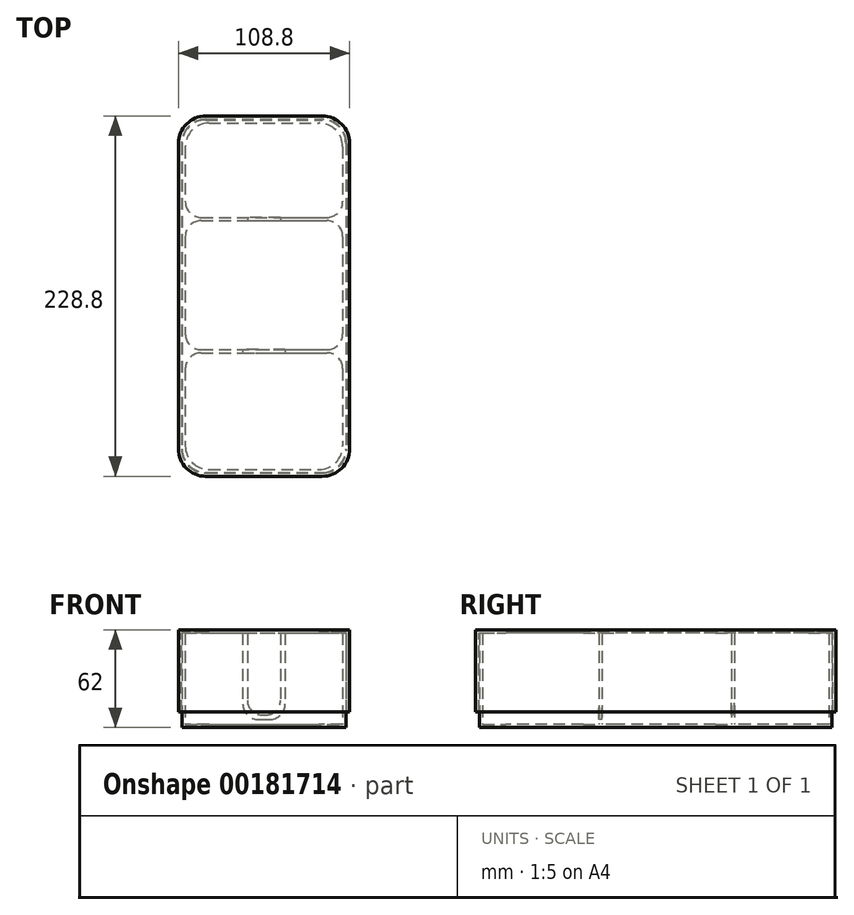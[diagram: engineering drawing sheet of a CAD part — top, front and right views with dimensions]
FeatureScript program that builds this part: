
annotation { "Feature Type Name" : "Feature", "Feature Type Description" : "" }
export const myFeature = defineFeature(function(context is Context, id is Id, definition is map)
    precondition{}
    {
        {
            var Q0;
            Q0=qCreatedBy(makeId("Top.planeOp"),FACE);
            var sketch = newSketch(context, id + "F0", { "sketchPlane" : qUnion([Q0])});
            skLineSegment(sketch, "E0.bottom", {"start": v(-39.51, 155.89) * mm, "end": v(30.49, 155.89) * mm});
            skLineSegment(sketch, "E0.top", {"start": v(-39.51, -64.11) * mm, "end": v(30.49, -64.11) * mm});
            skLineSegment(sketch, "E0.left", {"start": v(-54.51, 140.89) * mm, "end": v(-54.51, -49.11) * mm});
            skLineSegment(sketch, "E0.right", {"start": v(45.49, 140.89) * mm, "end": v(45.49, -49.11) * mm});
            skLineSegment(sketch, "E1", {"start": v(-54.51, 93.89) * mm, "end": v(45.49, 93.89) * mm});
            skLineSegment(sketch, "E2", {"start": v(-54.51, 11.89) * mm, "end": v(45.49, 11.89) * mm});
            skLineSegment(sketch, "E3.0", {"start": v(-56.51, 142.89) * mm, "end": v(-56.51, -51.11) * mm});
            skLineSegment(sketch, "E3.1", {"start": v(-41.51, 157.89) * mm, "end": v(32.49, 157.89) * mm});
            skLineSegment(sketch, "E3.2", {"start": v(47.49, 142.89) * mm, "end": v(47.49, -51.11) * mm});
            skLineSegment(sketch, "E3.3", {"start": v(-41.51, -66.11) * mm, "end": v(32.49, -66.11) * mm});
            skLineSegment(sketch, "E4.0", {"start": v(-54.51, 9.89) * mm, "end": v(45.49, 9.89) * mm});
            skLineSegment(sketch, "E5.0", {"start": v(-54.51, 95.89) * mm, "end": v(45.49, 95.89) * mm});
            skPoint(sketch, "E6.visualSharp", {"position": v(-54.51, 155.89) * mm});
            skArc(sketch, "E6.filletArc", {"start": v(-39.51, 155.89) * mm, "mid": v(-50.12, 151.5) * mm, "end": v(-54.51, 140.89) * mm});
            skPoint(sketch, "E7.visualSharp", {"position": v(45.49, 155.89) * mm});
            skArc(sketch, "E7.filletArc", {"start": v(45.49, 140.89) * mm, "mid": v(41.1, 151.5) * mm, "end": v(30.49, 155.89) * mm});
            skPoint(sketch, "E8.visualSharp", {"position": v(47.49, 157.89) * mm});
            skArc(sketch, "E8.filletArc", {"start": v(47.49, 142.89) * mm, "mid": v(43.1, 153.5) * mm, "end": v(32.49, 157.89) * mm});
            skPoint(sketch, "E9.visualSharp", {"position": v(45.49, -64.11) * mm});
            skArc(sketch, "E9.filletArc", {"start": v(30.49, -64.11) * mm, "mid": v(41.1, -59.72) * mm, "end": v(45.49, -49.11) * mm});
            skPoint(sketch, "E10.visualSharp", {"position": v(47.49, -66.11) * mm});
            skArc(sketch, "E10.filletArc", {"start": v(32.49, -66.11) * mm, "mid": v(43.1, -61.72) * mm, "end": v(47.49, -51.11) * mm});
            skPoint(sketch, "E11.visualSharp", {"position": v(-54.51, -64.11) * mm});
            skArc(sketch, "E11.filletArc", {"start": v(-54.51, -49.11) * mm, "mid": v(-50.12, -59.72) * mm, "end": v(-39.51, -64.11) * mm});
            skPoint(sketch, "E12.visualSharp", {"position": v(-56.51, -66.11) * mm});
            skArc(sketch, "E12.filletArc", {"start": v(-56.51, -51.11) * mm, "mid": v(-52.12, -61.72) * mm, "end": v(-41.51, -66.11) * mm});
            skPoint(sketch, "E13.visualSharp", {"position": v(-56.51, 157.89) * mm});
            skArc(sketch, "E13.filletArc", {"start": v(-41.51, 157.89) * mm, "mid": v(-52.12, 153.5) * mm, "end": v(-56.51, 142.89) * mm});
            skSolve(sketch);
        }
        {
            var Q0;
            {var subQ1=sQuery(id+"F0.wireOp",EDGE,"E0.bottom");Q0=makeQuery(id+"F0.imprint","IMPRINT",FACE,{"disambiguationData":[TD([[makeQuery(id+"F0.imprint","IMPRINT",EDGE,{"derivedFrom":subQ1}),1.0]])]});}
            var Q1;
            {var subQ0=sQuery(id+"F0.wireOp",EDGE,"E1");Q1=makeQuery(id+"F0.imprint","IMPRINT",FACE,{"disambiguationData":[TD([[makeQuery(id+"F0.imprint","IMPRINT",EDGE,{"derivedFrom":subQ0}),1.0]])]});}
            var Q2;
            {var subQ0=sQuery(id+"F0.wireOp",EDGE,"E2");Q2=makeQuery(id+"F0.imprint","IMPRINT",FACE,{"disambiguationData":[TD([[makeQuery(id+"F0.imprint","IMPRINT",EDGE,{"derivedFrom":subQ0}),-1.0]])]});}
            extrude(context, id + "F1", {"entities" : qUnion([Q0, Q1, Q2]), "depth" : 60 * mm});
        }
        {
            var Q0;
            {var subQ0=sQuery(id+"F0.wireOp",EDGE,"E0.bottom");Q0=makeQuery(id+"F0.imprint","IMPRINT",FACE,{"disambiguationData":[TD([[makeQuery(id+"F0.imprint","IMPRINT",EDGE,{"derivedFrom":subQ0}),-1.0]])]});}
            var Q1;
            {var subQ0=sQuery(id+"F0.wireOp",EDGE,"E1");Q1=makeQuery(id+"F0.imprint","IMPRINT",FACE,{"disambiguationData":[TD([[makeQuery(id+"F0.imprint","IMPRINT",EDGE,{"derivedFrom":subQ0}),-1.0]])]});}
            var Q2;
            {var subQ0=sQuery(id+"F0.wireOp",EDGE,"E0.top");Q2=makeQuery(id+"F0.imprint","IMPRINT",FACE,{"disambiguationData":[TD([[makeQuery(id+"F0.imprint","IMPRINT",EDGE,{"derivedFrom":subQ0}),1.0]])]});}
            extrude(context, id + "F2", {"entities" : qUnion([Q0, Q1, Q2]), "operationType" : NewBodyOperationType.ADD, "depth" : 2 * mm});
        }
        {
            var Q0;
            Q0=makeQuery(id+"F1.opExtrude","SWEPT_FACE",FACE,{"disambiguationData":[OSD([sQuery(id+"F0.wireOp",EDGE,"E4.0")])]});
            var sketch = newSketch(context, id + "F3", { "sketchPlane" : qUnion([Q0])});
            skLineSegment(sketch, "E14.bottom", {"start": v(-18.01, 60) * mm, "end": v(8.99, 60) * mm});
            skLineSegment(sketch, "E14.top", {"start": v(-8.01, 5) * mm, "end": v(-1.01, 5) * mm});
            skLineSegment(sketch, "E14.left", {"start": v(-18.01, 60) * mm, "end": v(-18.01, 15) * mm});
            skLineSegment(sketch, "E14.right", {"start": v(8.99, 60) * mm, "end": v(8.99, 15) * mm});
            skLineSegment(sketch, "E15", {"start": v(-4.51, 60) * mm, "end": v(-4.51, 2) * mm, "construction": true});
            skPoint(sketch, "E16.visualSharp", {"position": v(-18.01, 5) * mm});
            skArc(sketch, "E16.filletArc", {"start": v(-18.01, 15) * mm, "mid": v(-15.09, 7.93) * mm, "end": v(-8.01, 5) * mm});
            skPoint(sketch, "E17.visualSharp", {"position": v(8.99, 5) * mm});
            skArc(sketch, "E17.filletArc", {"start": v(-1.01, 5) * mm, "mid": v(6.06, 7.93) * mm, "end": v(8.99, 15) * mm});
            skSolve(sketch);
        }
        {
            var Q0;
            Q0=makeQuery(id+"F3.imprint","IMPRINT",FACE,{"disambiguationData":[TD([[makeQuery(id+"F3.imprint","IMPRINT",EDGE,{"derivedFrom":sQuery(id+"F3.wireOp",EDGE,"E14.bottom")}),-1.0]])]});
            extrude(context, id + "F4", {"entities" : qUnion([Q0]), "operationType" : NewBodyOperationType.REMOVE, "endBound" : BoundingType.UP_TO_NEXT, "oppositeDirection" : true, "depth" : 25 * mm});
        }
        {
            var Q0;
            Q0=makeQuery(id+"F1.opExtrude","SWEPT_FACE",FACE,{"disambiguationData":[OSD([sQuery(id+"F0.wireOp",EDGE,"E1")])]});
            var sketch = newSketch(context, id + "F5", { "sketchPlane" : qUnion([Q0])});
            skLineSegment(sketch, "E18", {"start": v(-4.51, 60) * mm, "end": v(-4.51, 2) * mm, "construction": true});
            skLineSegment(sketch, "E19.bottom", {"start": v(-15.01, 60) * mm, "end": v(5.99, 60) * mm});
            skLineSegment(sketch, "E19.top", {"start": v(-6.01, 8) * mm, "end": v(-3.01, 8) * mm});
            skLineSegment(sketch, "E19.left", {"start": v(-15.01, 60) * mm, "end": v(-15.01, 17) * mm});
            skLineSegment(sketch, "E19.right", {"start": v(5.99, 60) * mm, "end": v(5.99, 17) * mm});
            skPoint(sketch, "E20.visualSharp", {"position": v(-15.01, 8) * mm});
            skArc(sketch, "E20.filletArc", {"start": v(-15.01, 17) * mm, "mid": v(-12.38, 10.64) * mm, "end": v(-6.01, 8) * mm});
            skPoint(sketch, "E21.visualSharp", {"position": v(5.99, 8) * mm});
            skArc(sketch, "E21.filletArc", {"start": v(-3.01, 8) * mm, "mid": v(3.35, 10.64) * mm, "end": v(5.99, 17) * mm});
            skSolve(sketch);
        }
        {
            var Q0;
            Q0=makeQuery(id+"F5.imprint","IMPRINT",FACE,{"disambiguationData":[TD([[makeQuery(id+"F5.imprint","IMPRINT",EDGE,{"derivedFrom":sQuery(id+"F5.wireOp",EDGE,"E19.bottom")}),-1.0]])]});
            extrude(context, id + "F6", {"entities" : qUnion([Q0]), "operationType" : NewBodyOperationType.REMOVE, "endBound" : BoundingType.UP_TO_NEXT, "oppositeDirection" : true, "depth" : 25 * mm});
        }
        {
            var Q0;
            Q0=makeQuery(id+"F1.opExtrude","SWEPT_EDGE",EDGE,{"disambiguationData":[OSD([sQuery(id+"F0.wireOp",EDGE,"E0.left"),sQuery(id+"F0.wireOp",EDGE,"E4.0")])]});
            var Q1;
            Q1=makeQuery(id+"F1.opExtrude","SWEPT_EDGE",EDGE,{"disambiguationData":[OSD([sQuery(id+"F0.wireOp",EDGE,"E0.right"),sQuery(id+"F0.wireOp",EDGE,"E4.0")])]});
            var Q2;
            Q2=makeQuery(id+"F1.opExtrude","SWEPT_EDGE",EDGE,{"disambiguationData":[OSD([sQuery(id+"F0.wireOp",EDGE,"E0.left"),sQuery(id+"F0.wireOp",EDGE,"E2")])]});
            var Q3;
            Q3=makeQuery(id+"F1.opExtrude","SWEPT_EDGE",EDGE,{"disambiguationData":[OSD([sQuery(id+"F0.wireOp",EDGE,"E0.right"),sQuery(id+"F0.wireOp",EDGE,"E2")])]});
            var Q4;
            Q4=makeQuery(id+"F1.opExtrude","SWEPT_EDGE",EDGE,{"disambiguationData":[OSD([sQuery(id+"F0.wireOp",EDGE,"E0.left"),sQuery(id+"F0.wireOp",EDGE,"E1")])]});
            var Q5;
            Q5=makeQuery(id+"F1.opExtrude","SWEPT_EDGE",EDGE,{"disambiguationData":[OSD([sQuery(id+"F0.wireOp",EDGE,"E0.right"),sQuery(id+"F0.wireOp",EDGE,"E1")])]});
            var Q6;
            Q6=makeQuery(id+"F1.opExtrude","SWEPT_EDGE",EDGE,{"disambiguationData":[OSD([sQuery(id+"F0.wireOp",EDGE,"E0.right"),sQuery(id+"F0.wireOp",EDGE,"E5.0")])]});
            var Q7;
            Q7=makeQuery(id+"F1.opExtrude","SWEPT_EDGE",EDGE,{"disambiguationData":[OSD([sQuery(id+"F0.wireOp",EDGE,"E0.left"),sQuery(id+"F0.wireOp",EDGE,"E5.0")])]});
            fillet(context, id + "F7", {"entities" : qUnion([Q0, Q1, Q2, Q3, Q4, Q5, Q6, Q7]), "radius" : 10 * mm, "tangentPropagation" : true, "allowEdgeOverflow" : false});
        }
        {
            var Q0;
            Q0=makeQuery(id+"F1.opExtrude","CAP_FACE",FACE,{"disambiguationData":[OSD([sQuery(id+"F0.wireOp",EDGE,"E0.bottom"),sQuery(id+"F0.wireOp",EDGE,"E0.top"),sQuery(id+"F0.wireOp",EDGE,"E0.left"),sQuery(id+"F0.wireOp",EDGE,"E0.right"),sQuery(id+"F0.wireOp",EDGE,"E1"),sQuery(id+"F0.wireOp",EDGE,"E2"),sQuery(id+"F0.wireOp",EDGE,"E3.0"),sQuery(id+"F0.wireOp",EDGE,"E3.1"),sQuery(id+"F0.wireOp",EDGE,"E3.2"),sQuery(id+"F0.wireOp",EDGE,"E3.3"),sQuery(id+"F0.wireOp",EDGE,"E4.0"),sQuery(id+"F0.wireOp",EDGE,"E5.0"),sQuery(id+"F0.wireOp",EDGE,"E6.filletArc"),sQuery(id+"F0.wireOp",EDGE,"E7.filletArc"),sQuery(id+"F0.wireOp",EDGE,"E8.filletArc"),sQuery(id+"F0.wireOp",EDGE,"E9.filletArc"),sQuery(id+"F0.wireOp",EDGE,"E10.filletArc"),sQuery(id+"F0.wireOp",EDGE,"E11.filletArc"),sQuery(id+"F0.wireOp",EDGE,"E12.filletArc"),sQuery(id+"F0.wireOp",EDGE,"E13.filletArc")])],"isStart":false});
            var sketch = newSketch(context, id + "F8", { "sketchPlane" : qUnion([Q0])});
            skLineSegment(sketch, "E22.0", {"start": v(47.49, 142.89) * mm, "end": v(47.49, -51.11) * mm, "construction": true});
            skArc(sketch, "E23.0", {"start": v(47.49, 142.89) * mm, "mid": v(43.1, 153.5) * mm, "end": v(32.49, 157.89) * mm, "construction": true});
            skLineSegment(sketch, "E24.0", {"start": v(-41.51, 157.89) * mm, "end": v(32.49, 157.89) * mm, "construction": true});
            skArc(sketch, "E25.0", {"start": v(-41.51, 157.89) * mm, "mid": v(-52.12, 153.5) * mm, "end": v(-56.51, 142.89) * mm, "construction": true});
            skLineSegment(sketch, "E26.0", {"start": v(-56.51, 142.89) * mm, "end": v(-56.51, -51.11) * mm, "construction": true});
            skArc(sketch, "E27.0", {"start": v(-56.51, -51.11) * mm, "mid": v(-52.12, -61.72) * mm, "end": v(-41.51, -66.11) * mm, "construction": true});
            skLineSegment(sketch, "E28.0", {"start": v(-41.51, -66.11) * mm, "end": v(32.49, -66.11) * mm, "construction": true});
            skArc(sketch, "E29.0", {"start": v(32.49, -66.11) * mm, "mid": v(43.1, -61.72) * mm, "end": v(47.49, -51.11) * mm, "construction": true});
            skArc(sketch, "E30.0", {"start": v(-41.51, 158.29) * mm, "mid": v(-52.4, 153.78) * mm, "end": v(-56.91, 142.89) * mm});
            skLineSegment(sketch, "E30.1", {"start": v(-56.91, 142.89) * mm, "end": v(-56.91, -51.11) * mm});
            skLineSegment(sketch, "E30.2", {"start": v(-41.51, 158.29) * mm, "end": v(32.49, 158.29) * mm});
            skArc(sketch, "E30.3", {"start": v(-56.91, -51.11) * mm, "mid": v(-52.4, -62) * mm, "end": v(-41.51, -66.51) * mm});
            skArc(sketch, "E30.4", {"start": v(47.89, 142.89) * mm, "mid": v(43.38, 153.78) * mm, "end": v(32.49, 158.29) * mm});
            skLineSegment(sketch, "E30.5", {"start": v(47.89, 142.89) * mm, "end": v(47.89, -51.11) * mm});
            skArc(sketch, "E30.6", {"start": v(32.49, -66.51) * mm, "mid": v(43.38, -62) * mm, "end": v(47.89, -51.11) * mm});
            skLineSegment(sketch, "E30.7", {"start": v(-41.51, -66.51) * mm, "end": v(32.49, -66.51) * mm});
            skArc(sketch, "E31.0", {"start": v(-41.51, 160.29) * mm, "mid": v(-53.82, 155.2) * mm, "end": v(-58.91, 142.89) * mm});
            skLineSegment(sketch, "E31.1", {"start": v(-41.51, 160.29) * mm, "end": v(32.49, 160.29) * mm});
            skLineSegment(sketch, "E31.2", {"start": v(-58.91, 142.89) * mm, "end": v(-58.91, -51.11) * mm});
            skArc(sketch, "E31.3", {"start": v(49.89, 142.89) * mm, "mid": v(44.79, 155.2) * mm, "end": v(32.49, 160.29) * mm});
            skArc(sketch, "E31.4", {"start": v(-58.91, -51.11) * mm, "mid": v(-53.82, -63.42) * mm, "end": v(-41.51, -68.51) * mm});
            skLineSegment(sketch, "E31.5", {"start": v(-41.51, -68.51) * mm, "end": v(32.49, -68.51) * mm});
            skArc(sketch, "E31.6", {"start": v(32.49, -68.51) * mm, "mid": v(44.79, -63.42) * mm, "end": v(49.89, -51.11) * mm});
            skLineSegment(sketch, "E31.7", {"start": v(49.89, 142.89) * mm, "end": v(49.89, -51.11) * mm});
            skSolve(sketch);
        }
        {
            var Q0;
            {var subQ12=sQuery(id+"F0.wireOp",EDGE,"E0.bottom");Q0=makeQuery(id+"F8.imprint","IMPRINT",FACE,{"disambiguationData":[TD([[makeQuery(id+"F8.imprint","IMPRINT",EDGE,{"derivedFrom":makeQuery(id+"F1.opExtrude","CAP_EDGE",EDGE,{"disambiguationData":[OSD([subQ12])],"isStart":false})}),1.0]])]});}
            var Q1;
            {var subQ11=sQuery(id+"F0.wireOp",EDGE,"E0.bottom");Q1=makeQuery(id+"F8.imprint","IMPRINT",FACE,{"disambiguationData":[TD([[makeQuery(id+"F8.imprint","IMPRINT",EDGE,{"derivedFrom":makeQuery(id+"F1.opExtrude","CAP_EDGE",EDGE,{"disambiguationData":[OSD([subQ11])],"isStart":false})}),-1.0]])]});}
            var Q2;
            Q2=makeQuery(id+"F8.imprint","IMPRINT",FACE,{"disambiguationData":[TD([[makeQuery(id+"F8.imprint","IMPRINT",EDGE,{"derivedFrom":sQuery(id+"F8.wireOp",EDGE,"E30.0")}),-1.0]])]});
            var Q3;
            Q3=makeQuery(id+"F8.imprint","IMPRINT",FACE,{"disambiguationData":[TD([[makeQuery(id+"F8.imprint","IMPRINT",EDGE,{"derivedFrom":sQuery(id+"F8.wireOp",EDGE,"E30.0")}),1.0]])]});
            extrude(context, id + "F9", {"entities" : qUnion([Q0, Q1, Q2, Q3]), "depth" : 2 * mm});
        }
        {
            var Q0;
            Q0 = qSketchRegion(id + "F8", true);
            extrude(context, id + "F10", {"entities" : qUnion([Q0]), "operationType" : NewBodyOperationType.ADD, "oppositeDirection" : true, "depth" : 50 * mm});
        }
    });
